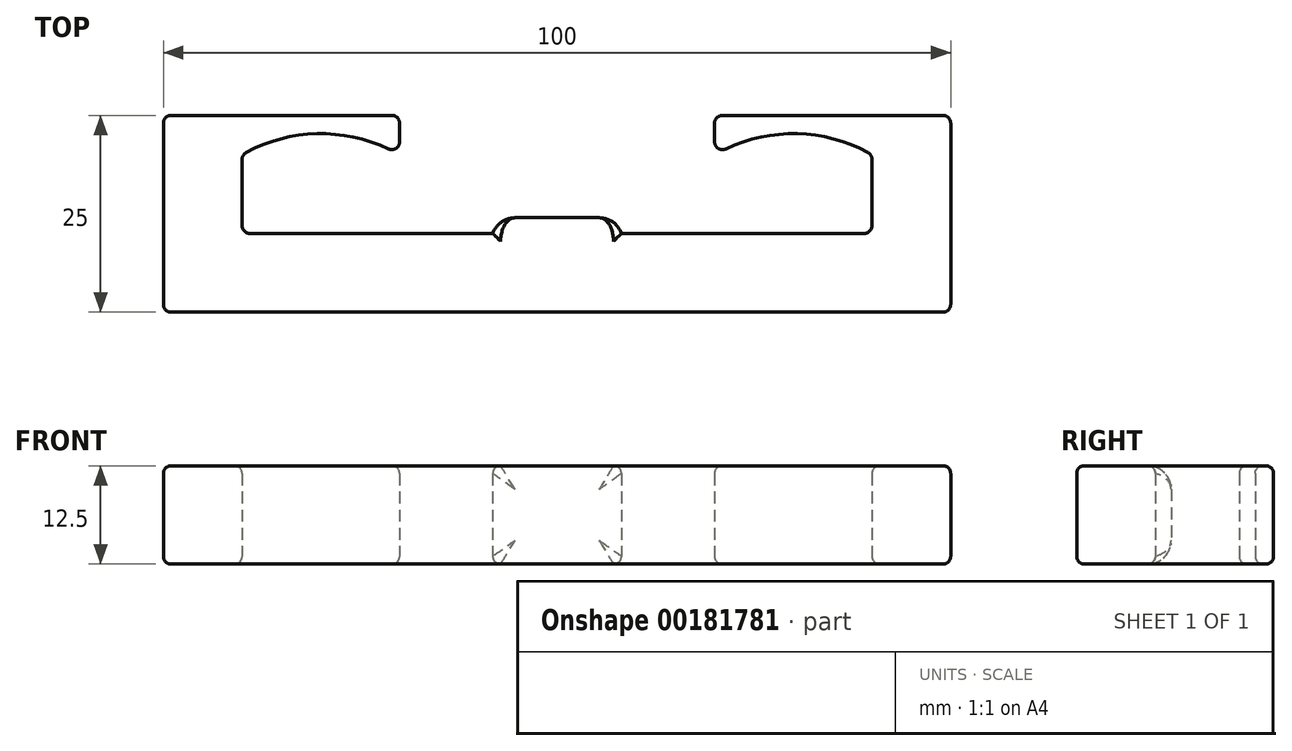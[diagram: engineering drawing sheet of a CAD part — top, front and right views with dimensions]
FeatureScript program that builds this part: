
annotation { "Feature Type Name" : "Feature", "Feature Type Description" : "" }
export const myFeature = defineFeature(function(context is Context, id is Id, definition is map)
    precondition{}
    {
        {
            var Q0;
            Q0=qCreatedBy(makeId("Top.planeOp"),FACE);
            var sketch = newSketch(context, id + "F0", { "sketchPlane" : qUnion([Q0])});
            skLineSegment(sketch, "E0", {"start": v(-44.84, 5) * mm, "end": v(-44.84, -20) * mm});
            skLineSegment(sketch, "E1", {"start": v(-44.84, -20) * mm, "end": v(5.16, -20) * mm});
            skLineSegment(sketch, "E2", {"start": v(5.16, -20) * mm, "end": v(5.16, -10) * mm});
            skLineSegment(sketch, "E3", {"start": v(-3.02, -10) * mm, "end": v(-34.84, -10) * mm});
            skLineSegment(sketch, "E4", {"start": v(-34.84, -10) * mm, "end": v(-34.84, 0) * mm});
            skLineSegment(sketch, "E5", {"start": v(-14.84, 0) * mm, "end": v(-14.84, 5) * mm});
            skLineSegment(sketch, "E6", {"start": v(-14.84, 5) * mm, "end": v(-44.84, 5) * mm});
            skArc(sketch, "E7", {"start": v(-14.84, 0) * mm, "mid": v(-24.84, 2.68) * mm, "end": v(-34.84, 0) * mm});
            skLineSegment(sketch, "E8", {"start": v(5.16, -43.28) * mm, "end": v(5.16, 39.42) * mm, "construction": true});
            skLineSegment(sketch, "E9.MirrorCS", {"start": v(13.33, -10) * mm, "end": v(45.16, -10) * mm});
            skLineSegment(sketch, "E10.MirrorCS", {"start": v(25.16, 0) * mm, "end": v(25.16, 5) * mm});
            skLineSegment(sketch, "E11.MirrorCS", {"start": v(45.16, -10) * mm, "end": v(45.16, 0) * mm});
            skLineSegment(sketch, "E12.MirrorCS", {"start": v(55.16, 5) * mm, "end": v(55.16, -20) * mm});
            skLineSegment(sketch, "E13.MirrorCS", {"start": v(25.16, 5) * mm, "end": v(55.16, 5) * mm});
            skLineSegment(sketch, "E14.MirrorCS", {"start": v(55.16, -20) * mm, "end": v(5.16, -20) * mm});
            skArc(sketch, "E15.MirrorCS", {"start": v(25.16, 0) * mm, "mid": v(35.16, 2.68) * mm, "end": v(45.16, 0) * mm});
            skLineSegment(sketch, "E16.bottom", {"start": v(-3.02, -8) * mm, "end": v(13.33, -8) * mm});
            skLineSegment(sketch, "E16.left", {"start": v(-3.02, -8) * mm, "end": v(-3.02, -10) * mm});
            skLineSegment(sketch, "E16.right", {"start": v(13.33, -8) * mm, "end": v(13.33, -10) * mm});
            skPoint(sketch, "E16.middle", {"position": v(5.16, -10) * mm});
            skPoint(sketch, "E17.orphan", {"position": v(-3.02, -12) * mm});
            skPoint(sketch, "E18.orphan", {"position": v(13.33, -12) * mm});
            skSolve(sketch);
        }
        {
            var Q0;
            Q0=makeQuery(id+"F0.imprint","IMPRINT",FACE,{"disambiguationData":[TD([[makeQuery(id+"F0.imprint","IMPRINT",EDGE,{"derivedFrom":sQuery(id+"F0.wireOp",EDGE,"E0")}),1.0]])]});
            extrude(context, id + "F1", {"entities" : qUnion([Q0]), "depth" : 12.5 * mm});
        }
        {
            var Q0;
            Q0=makeQuery(id+"F1.opExtrude","SWEPT_EDGE",EDGE,{"disambiguationData":[OSD([sQuery(id+"F0.wireOp",EDGE,"E5"),sQuery(id+"F0.wireOp",EDGE,"E7")])]});
            var Q1;
            Q1=makeQuery(id+"F1.opExtrude","CAP_EDGE",EDGE,{"disambiguationData":[OSD([sQuery(id+"F0.wireOp",EDGE,"E7")])],"isStart":false});
            var Q2;
            Q2=makeQuery(id+"F1.opExtrude","SWEPT_EDGE",EDGE,{"disambiguationData":[OSD([sQuery(id+"F0.wireOp",EDGE,"E12.MirrorCS"),sQuery(id+"F0.wireOp",EDGE,"E14.MirrorCS")])]});
            var Q3;
            Q3=makeQuery(id+"F1.opExtrude","SWEPT_EDGE",EDGE,{"disambiguationData":[OSD([sQuery(id+"F0.wireOp",EDGE,"E10.MirrorCS"),sQuery(id+"F0.wireOp",EDGE,"E13.MirrorCS")])]});
            var Q4;
            Q4=makeQuery(id+"F1.opExtrude","SWEPT_EDGE",EDGE,{"disambiguationData":[OSD([sQuery(id+"F0.wireOp",EDGE,"E0"),sQuery(id+"F0.wireOp",EDGE,"E6")])]});
            var Q5;
            Q5=makeQuery(id+"F1.opExtrude","SWEPT_EDGE",EDGE,{"disambiguationData":[OSD([sQuery(id+"F0.wireOp",EDGE,"E3"),sQuery(id+"F0.wireOp",EDGE,"E4")])]});
            var Q6;
            Q6=makeQuery(id+"F1.opExtrude","SWEPT_EDGE",EDGE,{"disambiguationData":[OSD([sQuery(id+"F0.wireOp",EDGE,"E5"),sQuery(id+"F0.wireOp",EDGE,"E6")])]});
            var Q7;
            Q7=makeQuery(id+"F1.opExtrude","SWEPT_EDGE",EDGE,{"disambiguationData":[OSD([sQuery(id+"F0.wireOp",EDGE,"E12.MirrorCS"),sQuery(id+"F0.wireOp",EDGE,"E13.MirrorCS")])]});
            var Q8;
            Q8=makeQuery(id+"F1.opExtrude","CAP_EDGE",EDGE,{"disambiguationData":[OSD([sQuery(id+"F0.wireOp",EDGE,"E1"),sQuery(id+"F0.wireOp",EDGE,"E14.MirrorCS")])],"isStart":false});
            var Q9;
            Q9=makeQuery(id+"F1.opExtrude","CAP_EDGE",EDGE,{"disambiguationData":[OSD([sQuery(id+"F0.wireOp",EDGE,"E15.MirrorCS")])],"isStart":false});
            var Q10;
            Q10=makeQuery(id+"F1.opExtrude","CAP_EDGE",EDGE,{"disambiguationData":[OSD([sQuery(id+"F0.wireOp",EDGE,"E12.MirrorCS")])],"isStart":true});
            var Q11;
            Q11=makeQuery(id+"F1.opExtrude","CAP_EDGE",EDGE,{"disambiguationData":[OSD([sQuery(id+"F0.wireOp",EDGE,"E16.right")])],"isStart":false});
            var Q12;
            Q12=makeQuery(id+"F1.opExtrude","CAP_EDGE",EDGE,{"disambiguationData":[OSD([sQuery(id+"F0.wireOp",EDGE,"E0")])],"isStart":true});
            var Q13;
            Q13=makeQuery(id+"F1.opExtrude","CAP_EDGE",EDGE,{"disambiguationData":[OSD([sQuery(id+"F0.wireOp",EDGE,"E16.right")])],"isStart":true});
            var Q14;
            Q14=makeQuery(id+"F1.opExtrude","CAP_EDGE",EDGE,{"disambiguationData":[OSD([sQuery(id+"F0.wireOp",EDGE,"E9.MirrorCS")])],"isStart":true});
            var Q15;
            Q15=makeQuery(id+"F1.opExtrude","CAP_EDGE",EDGE,{"disambiguationData":[OSD([sQuery(id+"F0.wireOp",EDGE,"E0")])],"isStart":false});
            var Q16;
            Q16=makeQuery(id+"F1.opExtrude","CAP_EDGE",EDGE,{"disambiguationData":[OSD([sQuery(id+"F0.wireOp",EDGE,"E10.MirrorCS")])],"isStart":true});
            var Q17;
            Q17=makeQuery(id+"F1.opExtrude","CAP_EDGE",EDGE,{"disambiguationData":[OSD([sQuery(id+"F0.wireOp",EDGE,"E10.MirrorCS")])],"isStart":false});
            var Q18;
            Q18=makeQuery(id+"F1.opExtrude","SWEPT_EDGE",EDGE,{"disambiguationData":[OSD([sQuery(id+"F0.wireOp",EDGE,"E11.MirrorCS"),sQuery(id+"F0.wireOp",EDGE,"E15.MirrorCS")])]});
            var Q19;
            Q19=makeQuery(id+"F1.opExtrude","CAP_EDGE",EDGE,{"disambiguationData":[OSD([sQuery(id+"F0.wireOp",EDGE,"E3")])],"isStart":false});
            var Q20;
            Q20=makeQuery(id+"F1.opExtrude","CAP_EDGE",EDGE,{"disambiguationData":[OSD([sQuery(id+"F0.wireOp",EDGE,"E1"),sQuery(id+"F0.wireOp",EDGE,"E14.MirrorCS")])],"isStart":true});
            var Q21;
            Q21=makeQuery(id+"F1.opExtrude","CAP_EDGE",EDGE,{"disambiguationData":[OSD([sQuery(id+"F0.wireOp",EDGE,"E9.MirrorCS")])],"isStart":false});
            var Q22;
            Q22=makeQuery(id+"F1.opExtrude","CAP_EDGE",EDGE,{"disambiguationData":[OSD([sQuery(id+"F0.wireOp",EDGE,"E16.left")])],"isStart":false});
            var Q23;
            Q23=makeQuery(id+"F1.opExtrude","CAP_EDGE",EDGE,{"disambiguationData":[OSD([sQuery(id+"F0.wireOp",EDGE,"E4")])],"isStart":true});
            var Q24;
            Q24=makeQuery(id+"F1.opExtrude","CAP_EDGE",EDGE,{"disambiguationData":[OSD([sQuery(id+"F0.wireOp",EDGE,"E3")])],"isStart":true});
            var Q25;
            Q25=makeQuery(id+"F1.opExtrude","SWEPT_EDGE",EDGE,{"disambiguationData":[OSD([sQuery(id+"F0.wireOp",EDGE,"E0"),sQuery(id+"F0.wireOp",EDGE,"E1")])]});
            var Q26;
            Q26=makeQuery(id+"F1.opExtrude","CAP_EDGE",EDGE,{"disambiguationData":[OSD([sQuery(id+"F0.wireOp",EDGE,"E12.MirrorCS")])],"isStart":false});
            var Q27;
            Q27=makeQuery(id+"F1.opExtrude","CAP_EDGE",EDGE,{"disambiguationData":[OSD([sQuery(id+"F0.wireOp",EDGE,"E13.MirrorCS")])],"isStart":true});
            var Q28;
            Q28=makeQuery(id+"F1.opExtrude","SWEPT_EDGE",EDGE,{"disambiguationData":[OSD([sQuery(id+"F0.wireOp",EDGE,"E4"),sQuery(id+"F0.wireOp",EDGE,"E7")])]});
            var Q29;
            Q29=makeQuery(id+"F1.opExtrude","SWEPT_EDGE",EDGE,{"disambiguationData":[OSD([sQuery(id+"F0.wireOp",EDGE,"E10.MirrorCS"),sQuery(id+"F0.wireOp",EDGE,"E15.MirrorCS")])]});
            var Q30;
            Q30=makeQuery(id+"F1.opExtrude","SWEPT_EDGE",EDGE,{"disambiguationData":[OSD([sQuery(id+"F0.wireOp",EDGE,"E9.MirrorCS"),sQuery(id+"F0.wireOp",EDGE,"E11.MirrorCS")])]});
            var Q31;
            Q31=makeQuery(id+"F1.opExtrude","CAP_EDGE",EDGE,{"disambiguationData":[OSD([sQuery(id+"F0.wireOp",EDGE,"E4")])],"isStart":false});
            var Q32;
            Q32=makeQuery(id+"F1.opExtrude","CAP_EDGE",EDGE,{"disambiguationData":[OSD([sQuery(id+"F0.wireOp",EDGE,"E13.MirrorCS")])],"isStart":false});
            var Q33;
            Q33=makeQuery(id+"F1.opExtrude","CAP_EDGE",EDGE,{"disambiguationData":[OSD([sQuery(id+"F0.wireOp",EDGE,"E5")])],"isStart":true});
            var Q34;
            Q34=makeQuery(id+"F1.opExtrude","CAP_EDGE",EDGE,{"disambiguationData":[OSD([sQuery(id+"F0.wireOp",EDGE,"E15.MirrorCS")])],"isStart":true});
            var Q35;
            Q35=makeQuery(id+"F1.opExtrude","CAP_EDGE",EDGE,{"disambiguationData":[OSD([sQuery(id+"F0.wireOp",EDGE,"E5")])],"isStart":false});
            var Q36;
            Q36=makeQuery(id+"F1.opExtrude","CAP_EDGE",EDGE,{"disambiguationData":[OSD([sQuery(id+"F0.wireOp",EDGE,"E6")])],"isStart":true});
            var Q37;
            Q37=makeQuery(id+"F1.opExtrude","CAP_EDGE",EDGE,{"disambiguationData":[OSD([sQuery(id+"F0.wireOp",EDGE,"E6")])],"isStart":false});
            var Q38;
            Q38=makeQuery(id+"F1.opExtrude","CAP_EDGE",EDGE,{"disambiguationData":[OSD([sQuery(id+"F0.wireOp",EDGE,"E7")])],"isStart":true});
            var Q39;
            Q39=makeQuery(id+"F1.opExtrude","CAP_EDGE",EDGE,{"disambiguationData":[OSD([sQuery(id+"F0.wireOp",EDGE,"E16.left")])],"isStart":true});
            var Q40;
            Q40=makeQuery(id+"F1.opExtrude","CAP_EDGE",EDGE,{"disambiguationData":[OSD([sQuery(id+"F0.wireOp",EDGE,"E11.MirrorCS")])],"isStart":false});
            var Q41;
            Q41=makeQuery(id+"F1.opExtrude","CAP_EDGE",EDGE,{"disambiguationData":[OSD([sQuery(id+"F0.wireOp",EDGE,"E11.MirrorCS")])],"isStart":true});
            fillet(context, id + "F2", {"entities" : qUnion([Q0, Q1, Q2, Q3, Q4, Q5, Q6, Q7, Q8, Q9, Q10, Q11, Q12, Q13, Q14, Q15, Q16, Q17, Q18, Q19, Q20, Q21, Q22, Q23, Q24, Q25, Q26, Q27, Q28, Q29, Q30, Q31, Q32, Q33, Q34, Q35, Q36, Q37, Q38, Q39, Q40, Q41]), "radius" : 1 * mm, "tangentPropagation" : true, "allowEdgeOverflow" : false});
        }
        {
            var Q0;
            Q0=makeQuery(id+"F1.opExtrude","SWEPT_FACE",FACE,{"disambiguationData":[OSD([sQuery(id+"F0.wireOp",EDGE,"E16.bottom")])]});
            fillet(context, id + "F3", {"entities" : qUnion([Q0]), "radius" : 3 * mm, "tangentPropagation" : true, "allowEdgeOverflow" : false});
        }
    });
